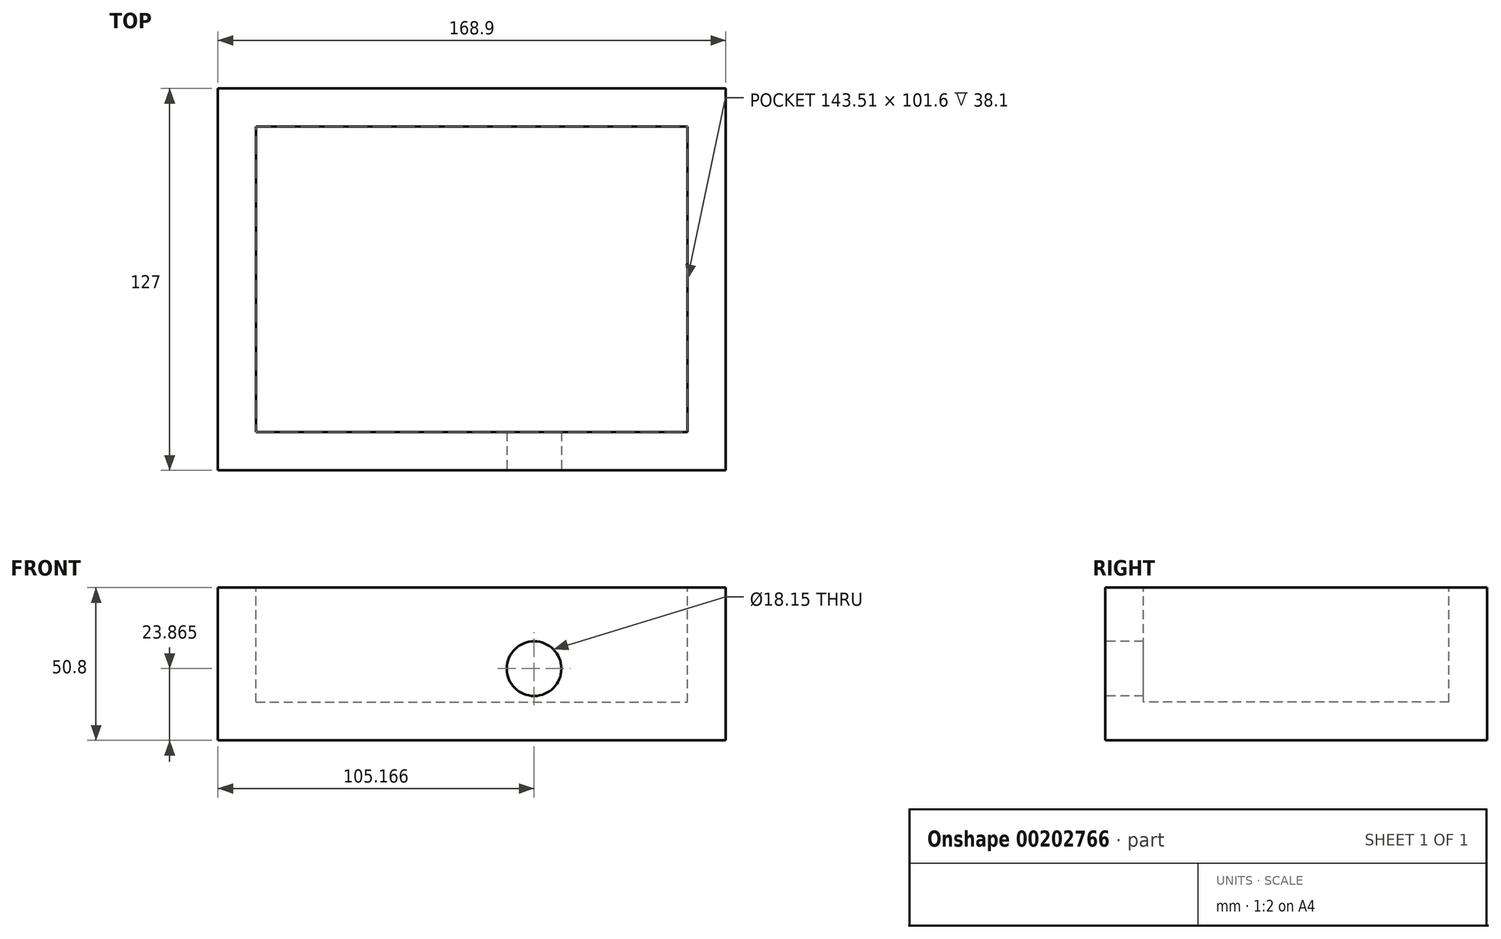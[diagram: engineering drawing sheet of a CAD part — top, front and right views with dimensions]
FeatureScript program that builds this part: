
annotation { "Feature Type Name" : "Feature", "Feature Type Description" : "" }
export const myFeature = defineFeature(function(context is Context, id is Id, definition is map)
    precondition{}
    {
        {
            var Q0;
            Q0=qCreatedBy(makeId("Top.planeOp"),FACE);
            var sketch = newSketch(context, id + "F0", { "sketchPlane" : qUnion([Q0])});
            skLineSegment(sketch, "E0.bottom", {"start": v(-84.45, 63.5) * mm, "end": v(84.46, 63.5) * mm});
            skLineSegment(sketch, "E0.top", {"start": v(-84.46, -63.5) * mm, "end": v(84.46, -63.5) * mm});
            skLineSegment(sketch, "E0.left", {"start": v(-84.46, 63.5) * mm, "end": v(-84.46, -63.5) * mm});
            skLineSegment(sketch, "E0.right", {"start": v(84.46, 63.5) * mm, "end": v(84.46, -63.5) * mm});
            skPoint(sketch, "E0.middle", {"position": v(0, 0) * mm});
            skSolve(sketch);
        }
        {
            var Q0;
            Q0=makeQuery(id+"F0.imprint","IMPRINT",FACE,{"disambiguationData":[TD([[makeQuery(id+"F0.imprint","IMPRINT",EDGE,{"derivedFrom":sQuery(id+"F0.wireOp",EDGE,"E0.bottom")}),-1.0]])]});
            extrude(context, id + "F1", {"entities" : qUnion([Q0]), "depth" : 50.8 * mm});
        }
        {
            var Q0;
            Q0=makeQuery(id+"F1.opExtrude","CAP_FACE",FACE,{"disambiguationData":[OSD([sQuery(id+"F0.wireOp",EDGE,"E0.bottom"),sQuery(id+"F0.wireOp",EDGE,"E0.top"),sQuery(id+"F0.wireOp",EDGE,"E0.left"),sQuery(id+"F0.wireOp",EDGE,"E0.right")])],"isStart":false});
            var sketch = newSketch(context, id + "F2", { "sketchPlane" : qUnion([Q0])});
            skLineSegment(sketch, "E1.bottom", {"start": v(-71.76, 50.8) * mm, "end": v(71.76, 50.8) * mm});
            skLineSegment(sketch, "E1.top", {"start": v(-71.76, -50.8) * mm, "end": v(71.76, -50.8) * mm});
            skLineSegment(sketch, "E1.left", {"start": v(-71.76, 50.8) * mm, "end": v(-71.76, -50.8) * mm});
            skLineSegment(sketch, "E1.right", {"start": v(71.76, 50.8) * mm, "end": v(71.76, -50.8) * mm});
            skPoint(sketch, "E1.middle", {"position": v(0, 0) * mm});
            skSolve(sketch);
        }
        {
            var Q0;
            Q0=makeQuery(id+"F2.imprint","IMPRINT",FACE,{"disambiguationData":[TD([[makeQuery(id+"F2.imprint","IMPRINT",EDGE,{"derivedFrom":sQuery(id+"F2.wireOp",EDGE,"E1.bottom")}),-1.0]])]});
            extrude(context, id + "F3", {"entities" : qUnion([Q0]), "operationType" : NewBodyOperationType.REMOVE, "oppositeDirection" : true, "depth" : 38.1 * mm});
        }
        {
            var Q0;
            Q0=makeQuery(id+"F1.opExtrude","SWEPT_FACE",FACE,{"disambiguationData":[OSD([sQuery(id+"F0.wireOp",EDGE,"E0.top")])]});
            var sketch = newSketch(context, id + "F4", { "sketchPlane" : qUnion([Q0])});
            skCircle(sketch, "E2", {"center": v(20.72, 23.86) * mm, "radius": 9.08 * mm});
            skSolve(sketch);
        }
        {
            var Q0;
            Q0=makeQuery(id+"F4.imprint","IMPRINT",FACE,{"disambiguationData":[TD([[makeQuery(id+"F4.imprint","IMPRINT",EDGE,{"derivedFrom":sQuery(id+"F4.wireOp",EDGE,"E2")}),1.0]])]});
            extrude(context, id + "F5", {"entities" : qUnion([Q0]), "operationType" : NewBodyOperationType.REMOVE, "oppositeDirection" : true, "depth" : 25.4 * mm});
        }
    });
